# Revit family: Model-904
name_source: partatom
category: Doors
units: mm (PartAtom-declared; Revit-internal decimal feet)

## family parameters
Always vertical = Yes
Cut with Voids When Loaded = No
Host = Wall
OmniClass Number = 23.30.10.17.37.14
OmniClass Title = Sectional Overhead Doors
Room Calculation Point = No
Shared = No

## types (1)
- By Type
    Assembly Code = B2030410
    Bottom Section Panel Material = Glass
    CAD and Specifications = http://www.clopaydoor.com
    Description = 2-1/8" Thick Aluminum Sectional Door
    Door Height = 12' - 0"
    Door Width = 12' - 4"
    Double End Stiles = No
    Double Torsion Shaft = No
    File Revision = 00 (June, 2010)
    FloorToTopSctn = 10' - 0"
    Frame Finish = Aluminum
    Frame Material = Anodized Aluminum
    Function = Interior
    Hardware = 14 ga. min. steel hinges; 10-ball steel rollers
    Height = 12' - 0"
    High Lift = 4' - 0"
    Insulation = Expanded polyurethane
    Keynote = 08 36 13
    LEED = http://products.construction.com
    Manufacturer = Clopay Building Products Company
    Manufacturer Website = http://www.clopaydoor.com
    Maximum Size = 20' 2'' wide by 20' 0'' high. Additional limitations may apply do to door weight or glazing type. Consult Clopay for specificiations and shop drawings.
    Model = 902
    NumIntSections = 4
    NumSections = 6
    NumSectionsNotRounded = 6
    Omniclass Table = 23-30 10 17 37
    Opener - Jackshaft Left Side = No
    Opener - Jackshaft Right Side = No
    Opener - Trolley = No
    Opening Height = 12' - 0"
    Opening Width = 12' - 2"
    Overlap = 0' - 1"
    Overlapping Jamb = Yes
    Product Features and Benefits = http://www.clopaydoor.com
    R-Value = 3.8 (with clear insulated glass)
    Roof Pitch = 0
    Rough Height = 0' - 0"
    Rough Width = 0' - 0"
    Sales Information = http://www.clopaydoor.com
    Section Height = 2' - 0"
    Spec Wizard = http://www.arcat.com
    Thickness = 0' - 2 1/8"
    Track = Galvanized steel (gauge varies according to door size)
    Track Type = Track - Standard Lift : 15" Radius
    URL = www.clopaydoor.com
    Upper Sections Panel Material = Glass
    VisArray = Yes
    VisSection2 = No
    Wall Closure = By host
    Width = 12' - 2"
    Windload = Doors available rated for various design pressures; consult Clopay for avaialbility and specifications

## geometry (parser evidence)
native form markers: Blend x2, Sweep x44
no freeform markers — native parametric forms only
